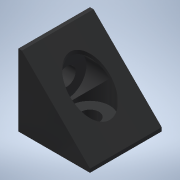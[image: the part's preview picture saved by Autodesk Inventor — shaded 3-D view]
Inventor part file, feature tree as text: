
AUTODESK INVENTOR PART (.ipt)
format: ipt  version: 2022 (Build 260153000, 153)  size: 125,952 bytes
history: native  units: in
note: dims shown in document units (in); Inventor stores cm internally (conversion verified against a paired STEP export)
features: extrude x5, sketch x5
ambient origin geometry x8: Origin, YZ Plane, XZ Plane, XY Plane, X Axis, Y Axis, Z Axis, Center Point
bodies: Solid1 (feature_tree)
feature tree (10):
  extrude  "Extrusion1"  Depth=0.7874in
  extrude  "Extrusion2"  Depth=0.7874in
  extrude  "Extrusion3"  Depth=0.7874in
  extrude  "Extrusion4"  Depth=0.1378in
  extrude  "Extrusion5"  Depth=0.1378in
  sketch  "Sketch1"  dims[d0=135.0deg d1=0.7874in]
  sketch  "Sketch2"  dims[d2=0.7874in d3=0.0394in]
  sketch  "Sketch3"  dims[d4=0.7874in d5=0.0in d6=0.1969in]
  sketch  "Sketch4"  dims[d7=0.1378in d8=0.0in d9=0.4331in]
  sketch  "Sketch5"  dims[d10=0.1378in d11=0.0in d12=0.1969in d13=0.1378in d14=0.0in d15=0.4331in d16=0.1378in d17=0.0in]
